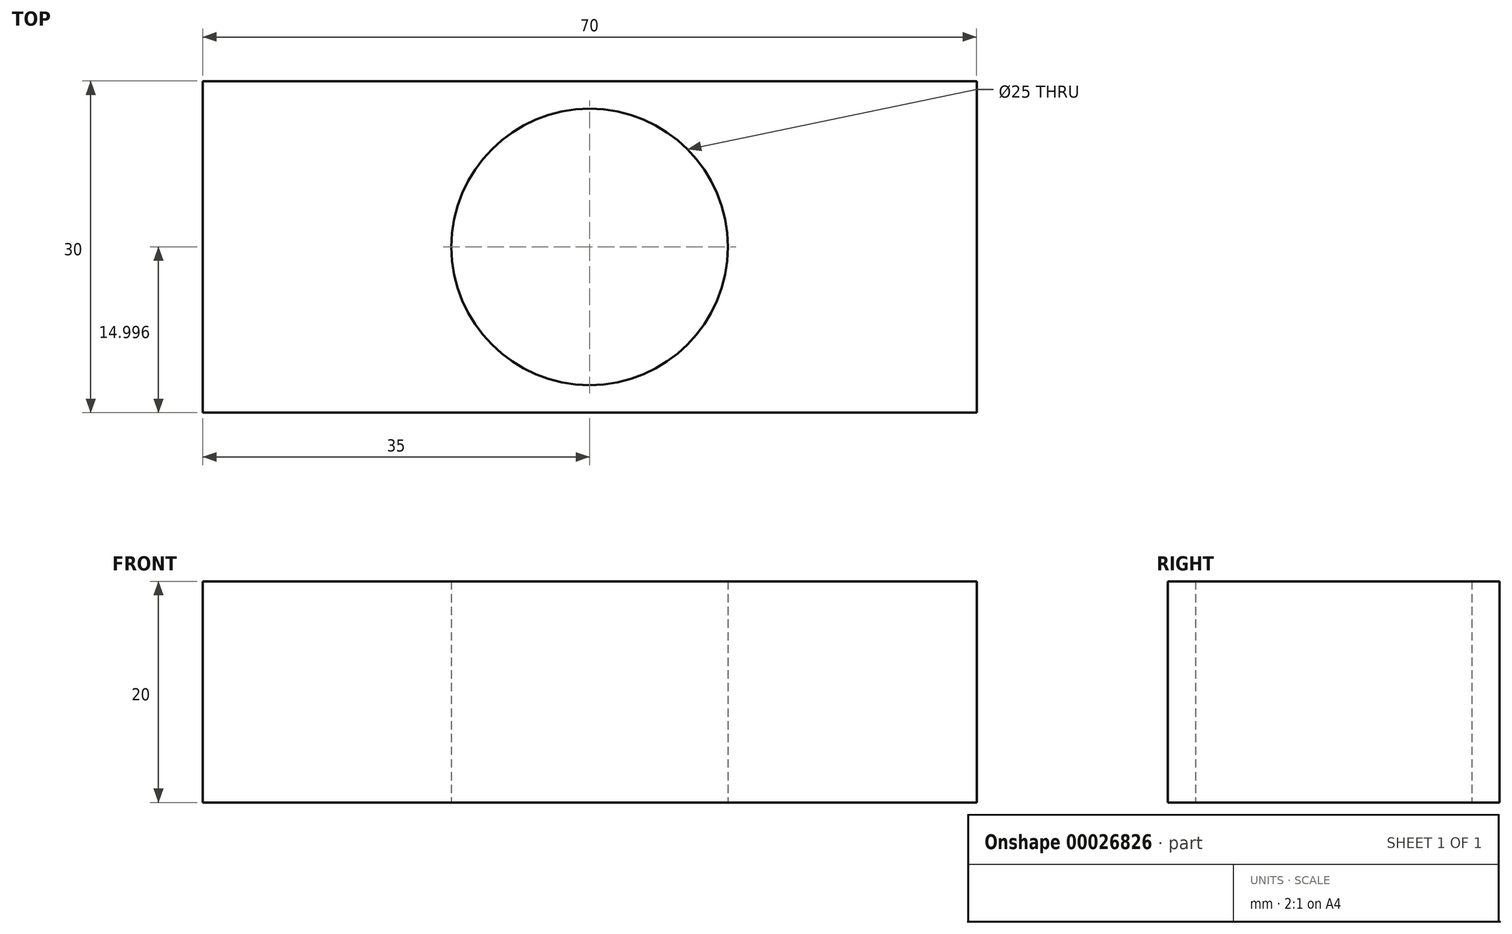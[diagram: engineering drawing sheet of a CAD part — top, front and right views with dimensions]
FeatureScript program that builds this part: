
annotation { "Feature Type Name" : "Feature", "Feature Type Description" : "" }
export const myFeature = defineFeature(function(context is Context, id is Id, definition is map)
    precondition{}
    {
        {
            var Q0;
            Q0=qCreatedBy(makeId("Top.planeOp"),FACE);
            var sketch = newSketch(context, id + "F0", { "sketchPlane" : qUnion([Q0])});
            skLineSegment(sketch, "E0.rect.bottom", {"start": v(-35.26, 11.2) * mm, "end": v(34.74, 11.2) * mm});
            skLineSegment(sketch, "E0.rect.top", {"start": v(-35.26, -18.8) * mm, "end": v(34.74, -18.8) * mm});
            skLineSegment(sketch, "E0.rect.left", {"start": v(-35.26, 11.2) * mm, "end": v(-35.26, -18.8) * mm});
            skLineSegment(sketch, "E0.rect.right", {"start": v(34.74, 11.2) * mm, "end": v(34.74, -18.8) * mm});
            skPoint(sketch, "E0.rect.middle", {"position": v(-0.26, -3.8) * mm});
            skLineSegment(sketch, "E1", {"start": v(34.74, -18.8) * mm, "end": v(34.74, -3.8) * mm});
            skLineSegment(sketch, "E2", {"start": v(34.74, -3.8) * mm, "end": v(-35.26, -3.8) * mm});
            skCircle(sketch, "E3", {"center": v(-0.26, -3.8) * mm, "radius": 12.5 * mm});
            skSolve(sketch);
        }
        {
            var Q0;
            {var subQ7=sQuery(id+"F0.wireOp",EDGE,"E0.rect.top");Q0=makeQuery(id+"F0.imprint","IMPRINT",FACE,{"disambiguationData":[TD([[makeQuery(id+"F0.imprint","IMPRINT",EDGE,{"derivedFrom":subQ7}),1.0]])]});}
            var Q1;
            {var subQ7=sQuery(id+"F0.wireOp",EDGE,"E0.rect.bottom");Q1=makeQuery(id+"F0.imprint","IMPRINT",FACE,{"disambiguationData":[TD([[makeQuery(id+"F0.imprint","IMPRINT",EDGE,{"derivedFrom":subQ7}),-1.0]])]});}
            extrude(context, id + "F1", {"entities" : qUnion([Q0, Q1]), "depth" : 20 * mm});
        }
    });
